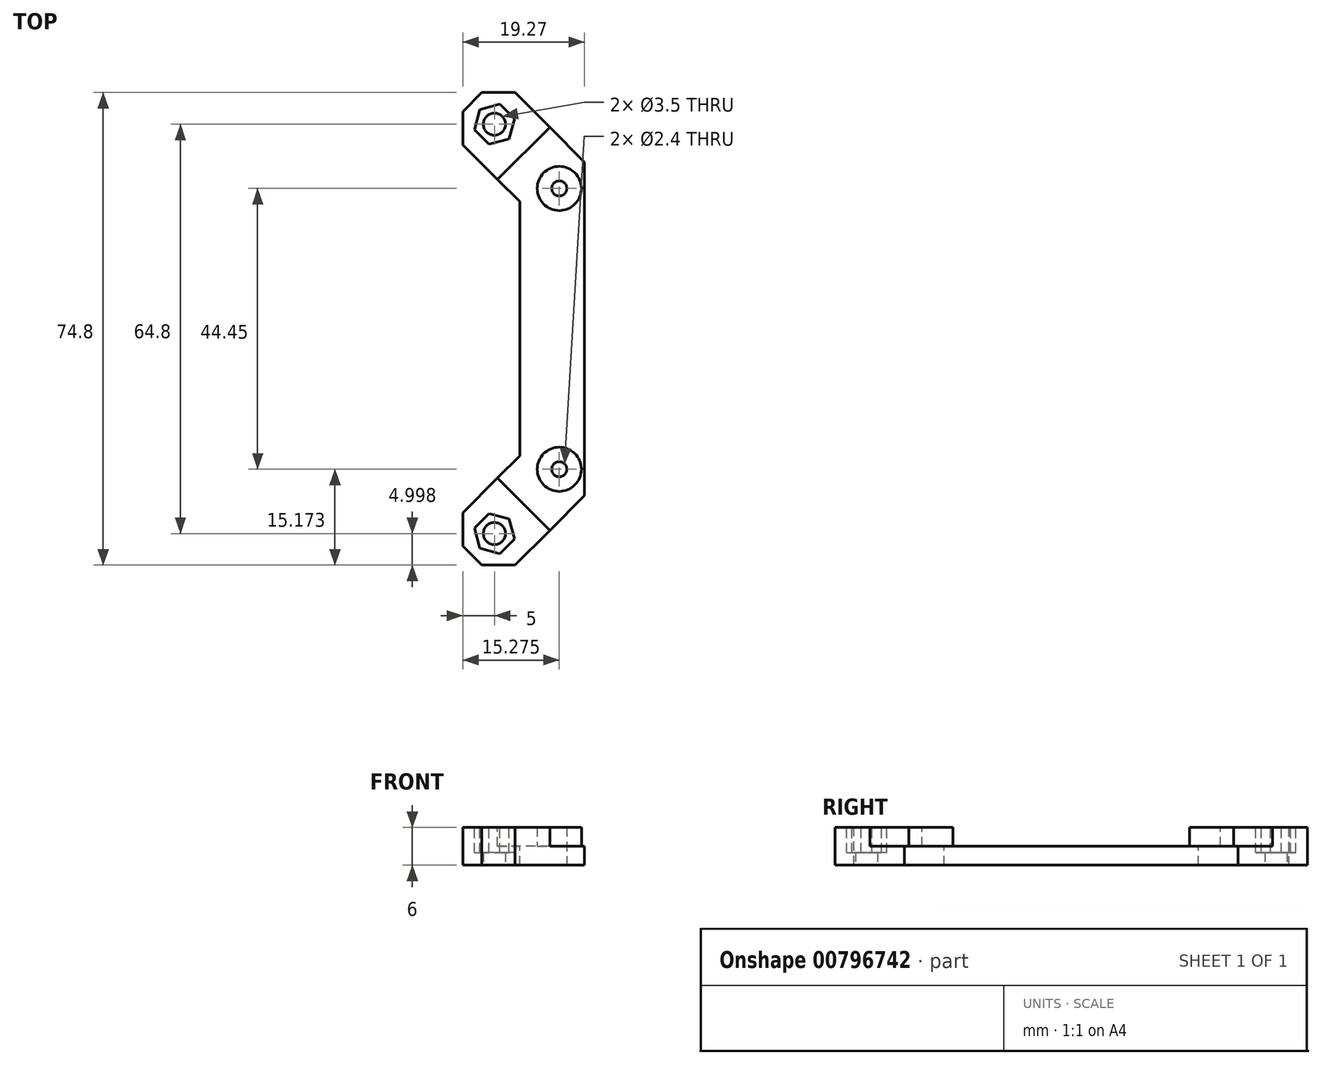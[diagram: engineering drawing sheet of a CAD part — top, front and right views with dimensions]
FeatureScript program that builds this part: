
annotation { "Feature Type Name" : "Feature", "Feature Type Description" : "" }
export const myFeature = defineFeature(function(context is Context, id is Id, definition is map)
    precondition{}
    {
        {
            var Q0;
            Q0=qCreatedBy(makeId("Top.planeOp"),FACE);
            var sketch = newSketch(context, id + "F0", { "sketchPlane" : qUnion([Q0])});
            skLineSegment(sketch, "E0.bottom", {"start": v(-40.3, 34.1) * mm, "end": v(54.94, 34.1) * mm, "construction": true});
            skLineSegment(sketch, "E0.top", {"start": v(-40.3, -10.36) * mm, "end": v(54.94, -10.36) * mm, "construction": true});
            skLineSegment(sketch, "E0.left", {"start": v(-40.3, 34.1) * mm, "end": v(-40.3, -10.36) * mm, "construction": true});
            skLineSegment(sketch, "E0.right", {"start": v(54.94, 34.1) * mm, "end": v(54.94, -10.36) * mm, "construction": true});
            skCircle(sketch, "E1", {"center": v(-40.3, -10.36) * mm, "radius": 1.2 * mm});
            skCircle(sketch, "E2", {"center": v(-40.3, 34.1) * mm, "radius": 1.2 * mm});
            skCircle(sketch, "E3", {"center": v(54.94, 34.1) * mm, "radius": 1.75 * mm});
            skCircle(sketch, "E4", {"center": v(54.94, -10.36) * mm, "radius": 1.75 * mm});
            skLineSegment(sketch, "E5.bottom", {"start": v(-50.58, 44.27) * mm, "end": v(65.22, 44.27) * mm, "construction": true});
            skLineSegment(sketch, "E5.top", {"start": v(-50.58, -20.53) * mm, "end": v(65.22, -20.53) * mm, "construction": true});
            skLineSegment(sketch, "E5.left", {"start": v(-50.58, 44.27) * mm, "end": v(-50.58, -20.53) * mm, "construction": true});
            skLineSegment(sketch, "E5.right", {"start": v(65.22, 44.27) * mm, "end": v(65.22, -20.53) * mm, "construction": true});
            skLineSegment(sketch, "E6", {"start": v(54.94, 11.87) * mm, "end": v(65.22, 11.87) * mm, "construction": true});
            skLineSegment(sketch, "E7", {"start": v(-50.58, 11.87) * mm, "end": v(-40.3, 11.87) * mm, "construction": true});
            skCircle(sketch, "E8", {"center": v(-50.58, -20.53) * mm, "radius": 1.75 * mm});
            skCircle(sketch, "E9", {"center": v(-50.58, 44.27) * mm, "radius": 1.75 * mm});
            skCircle(sketch, "E10", {"center": v(65.22, 44.27) * mm, "radius": 1.75 * mm});
            skCircle(sketch, "E11", {"center": v(65.22, -20.53) * mm, "radius": 1.75 * mm});
            skLineSegment(sketch, "E12", {"start": v(-55.58, 49.27) * mm, "end": v(-55.58, -25.53) * mm});
            skLineSegment(sketch, "E13", {"start": v(-55.58, -25.53) * mm, "end": v(-36.3, -25.53) * mm});
            skLineSegment(sketch, "E14", {"start": v(-36.3, -25.53) * mm, "end": v(-36.3, 49.27) * mm});
            skLineSegment(sketch, "E15", {"start": v(-36.3, 49.27) * mm, "end": v(-55.58, 49.27) * mm});
            skLineSegment(sketch, "E16", {"start": v(-55.58, 11.87) * mm, "end": v(-50.58, 11.87) * mm, "construction": true});
            skSolve(sketch);
        }
        {
            var Q0;
            Q0=makeQuery(id+"F0.imprint","IMPRINT",FACE,{"disambiguationData":[TD([[makeQuery(id+"F0.imprint","IMPRINT",EDGE,{"derivedFrom":sQuery(id+"F0.wireOp",EDGE,"E1")}),-1.0]])]});
            extrude(context, id + "F1", {"entities" : qUnion([Q0]), "depth" : 6 * mm, "offsetDistance" : 25 * mm});
        }
        {
            var Q0;
            Q0=makeQuery(id+"F1.opExtrude","CAP_FACE",FACE,{"disambiguationData":[OSD([sQuery(id+"F0.wireOp",EDGE,"E1"),sQuery(id+"F0.wireOp",EDGE,"E2"),sQuery(id+"F0.wireOp",EDGE,"E8"),sQuery(id+"F0.wireOp",EDGE,"E9"),sQuery(id+"F0.wireOp",EDGE,"E12"),sQuery(id+"F0.wireOp",EDGE,"E13"),sQuery(id+"F0.wireOp",EDGE,"E14"),sQuery(id+"F0.wireOp",EDGE,"E15")])],"isStart":false});
            var sketch = newSketch(context, id + "F2", { "sketchPlane" : qUnion([Q0])});
            skLineSegment(sketch, "E17", {"start": v(-55.58, -17.26) * mm, "end": v(-46.58, -8.26) * mm});
            skLineSegment(sketch, "E18", {"start": v(-46.58, -8.26) * mm, "end": v(-46.58, 32) * mm});
            skLineSegment(sketch, "E19", {"start": v(-46.58, 32) * mm, "end": v(-55.58, 41) * mm});
            skLineSegment(sketch, "E20", {"start": v(-46.58, 11.87) * mm, "end": v(-55.58, 11.87) * mm, "construction": true});
            skLineSegment(sketch, "E21", {"start": v(-36.3, 38.27) * mm, "end": v(-47.3, 49.27) * mm});
            skLineSegment(sketch, "E22", {"start": v(-47.3, -25.53) * mm, "end": v(-36.3, -14.53) * mm});
            skLineSegment(sketch, "E23", {"start": v(-41.8, 43.77) * mm, "end": v(-50.08, 35.5) * mm});
            skLineSegment(sketch, "E24", {"start": v(-41.8, -20.03) * mm, "end": v(-50.08, -11.76) * mm});
            skCircle(sketch, "E25.cCircle", {"center": v(-50.58, 44.27) * mm, "radius": 2.85 * mm, "construction": true});
            skLineSegment(sketch, "E25.0", {"start": v(-52.9, 46.6) * mm, "end": v(-49.73, 47.45) * mm});
            skLineSegment(sketch, "E25.1", {"start": v(-49.73, 47.45) * mm, "end": v(-47.4, 45.12) * mm});
            skLineSegment(sketch, "E25.2", {"start": v(-47.4, 45.12) * mm, "end": v(-48.25, 41.94) * mm});
            skLineSegment(sketch, "E25.3", {"start": v(-48.25, 41.94) * mm, "end": v(-51.43, 41.09) * mm});
            skLineSegment(sketch, "E25.4", {"start": v(-51.43, 41.09) * mm, "end": v(-53.76, 43.42) * mm});
            skLineSegment(sketch, "E25.5", {"start": v(-53.76, 43.42) * mm, "end": v(-52.9, 46.6) * mm});
            skPoint(sketch, "E25.0.midPoint", {"position": v(-51.32, 47.02) * mm});
            skLineSegment(sketch, "E26", {"start": v(-52.9, 46.6) * mm, "end": v(-55.58, 49.27) * mm, "construction": true});
            skCircle(sketch, "E27.cCircle", {"center": v(-50.58, -20.53) * mm, "radius": 2.85 * mm, "construction": true});
            skLineSegment(sketch, "E27.0", {"start": v(-49.73, -23.71) * mm, "end": v(-52.9, -22.86) * mm});
            skLineSegment(sketch, "E27.1", {"start": v(-52.9, -22.86) * mm, "end": v(-53.76, -19.68) * mm});
            skLineSegment(sketch, "E27.2", {"start": v(-53.76, -19.68) * mm, "end": v(-51.43, -17.35) * mm});
            skLineSegment(sketch, "E27.3", {"start": v(-51.43, -17.35) * mm, "end": v(-48.25, -18.2) * mm});
            skLineSegment(sketch, "E27.4", {"start": v(-48.25, -18.2) * mm, "end": v(-47.4, -21.38) * mm});
            skLineSegment(sketch, "E27.5", {"start": v(-47.4, -21.38) * mm, "end": v(-49.73, -23.71) * mm});
            skPoint(sketch, "E27.0.midPoint", {"position": v(-51.32, -23.28) * mm});
            skLineSegment(sketch, "E28", {"start": v(-52.9, -22.86) * mm, "end": v(-55.58, -25.53) * mm, "construction": true});
            skSolve(sketch);
        }
        {
            var Q0;
            {var subQ0=sQuery(id+"F2.wireOp",EDGE,"E21");var subQ1=makeQuery(id+"F1.opExtrude","CAP_EDGE",EDGE,{"disambiguationData":[OSD([sQuery(id+"F0.wireOp",EDGE,"E14")])],"isStart":false});var subQ2=makeQuery(id+"F2.imprint","INTERSECT",VERTEX,{"derivedFrom":[subQ1,subQ0]});Q0=makeQuery(id+"F2.imprint","IMPRINT",FACE,{"disambiguationData":[TD([[makeQuery(id+"F2.imprint","IMPRINT",EDGE,{"disambiguationData":[TD([[subQ2,-1.0]])],"derivedFrom":subQ0}),-1.0]])]});}
            var Q1;
            {var subQ1=sQuery(id+"F2.wireOp",EDGE,"E18");Q1=makeQuery(id+"F2.imprint","IMPRINT",FACE,{"disambiguationData":[TD([[makeQuery(id+"F2.imprint","IMPRINT",EDGE,{"derivedFrom":subQ1}),1.0]])]});}
            var Q2;
            {var subQ0=sQuery(id+"F2.wireOp",EDGE,"E22");var subQ1=makeQuery(id+"F1.opExtrude","CAP_EDGE",EDGE,{"disambiguationData":[OSD([sQuery(id+"F0.wireOp",EDGE,"E13")])],"isStart":false});var subQ2=makeQuery(id+"F2.imprint","INTERSECT",VERTEX,{"derivedFrom":[subQ1,subQ0]});Q2=makeQuery(id+"F2.imprint","IMPRINT",FACE,{"disambiguationData":[TD([[makeQuery(id+"F2.imprint","IMPRINT",EDGE,{"disambiguationData":[TD([[subQ2,-1.0]])],"derivedFrom":subQ0}),-1.0]])]});}
            extrude(context, id + "F3", {"entities" : qUnion([Q0, Q1, Q2]), "operationType" : NewBodyOperationType.REMOVE, "oppositeDirection" : true, "depth" : 25 * mm, "offsetDistance" : 25 * mm});
        }
        {
            var Q0;
            {var subQ5=sQuery(id+"F2.wireOp",EDGE,"E18");Q0=makeQuery(id+"F2.imprint","IMPRINT",FACE,{"disambiguationData":[TD([[makeQuery(id+"F2.imprint","IMPRINT",EDGE,{"derivedFrom":subQ5}),-1.0]])]});}
            var Q1;
            Q1=makeQuery(id+"F2.imprint","IMPRINT",FACE,{"disambiguationData":[TD([[makeQuery(id+"F2.imprint","IMPRINT",EDGE,{"derivedFrom":sQuery(id+"F2.wireOp",EDGE,"d42421a5-ac7b-4057-9577-e83b0d60c713.0")}),-1.0]])]});
            var Q2;
            Q2=makeQuery(id+"F2.imprint","IMPRINT",FACE,{"disambiguationData":[TD([[makeQuery(id+"F2.imprint","IMPRINT",EDGE,{"derivedFrom":sQuery(id+"F2.wireOp",EDGE,"defd8206-cf14-4cda-9da2-6035153b5954.0")}),-1.0]])]});
            extrude(context, id + "F4", {"entities" : qUnion([Q0, Q1, Q2]), "operationType" : NewBodyOperationType.REMOVE, "oppositeDirection" : true, "depth" : 3 * mm, "offsetDistance" : 25 * mm});
        }
        {
            var Q0;
            Q0=makeQuery(id+"F1.opExtrude","SWEPT_EDGE",EDGE,{"disambiguationData":[OSD([sQuery(id+"F0.wireOp",EDGE,"E12"),sQuery(id+"F0.wireOp",EDGE,"E15")])]});
            var Q1;
            Q1=makeQuery(id+"F1.opExtrude","SWEPT_EDGE",EDGE,{"disambiguationData":[OSD([sQuery(id+"F0.wireOp",EDGE,"E12"),sQuery(id+"F0.wireOp",EDGE,"E13")])]});
            chamfer(context, id + "F5", {"entities" : qUnion([Q0, Q1]), "width" : 3 * mm, "tangentPropagation" : true});
        }
        {
            var Q0;
            Q0=makeQuery(id+"F2.imprint","IMPRINT",FACE,{"disambiguationData":[TD([[makeQuery(id+"F2.imprint","IMPRINT",EDGE,{"derivedFrom":sQuery(id+"F2.wireOp",EDGE,"E25.0")}),-1.0]])]});
            var Q1;
            Q1=makeQuery(id+"F2.imprint","IMPRINT",FACE,{"disambiguationData":[TD([[makeQuery(id+"F2.imprint","IMPRINT",EDGE,{"derivedFrom":sQuery(id+"F2.wireOp",EDGE,"E27.0")}),-1.0]])]});
            extrude(context, id + "F6", {"entities" : qUnion([Q0, Q1]), "operationType" : NewBodyOperationType.REMOVE, "oppositeDirection" : true, "depth" : 4 * mm, "offsetDistance" : 25 * mm});
        }
        {
            var Q0;
            Q0=makeQuery(id+"F4.boolean.opBoolean","COPY",FACE,{"derivedFrom":makeQuery(id+"F4.opExtrude","CAP_FACE",FACE,{"disambiguationData":[OSD([sQuery(id+"F0.wireOp",EDGE,"E1"),sQuery(id+"F0.wireOp",EDGE,"E2"),sQuery(id+"F0.wireOp",EDGE,"E14"),sQuery(id+"F2.wireOp",EDGE,"E17"),sQuery(id+"F2.wireOp",EDGE,"E18"),sQuery(id+"F2.wireOp",EDGE,"E19"),sQuery(id+"F2.wireOp",EDGE,"E21"),sQuery(id+"F2.wireOp",EDGE,"E22"),sQuery(id+"F2.wireOp",EDGE,"E23"),sQuery(id+"F2.wireOp",EDGE,"E24")])],"isStart":false})});
            var sketch = newSketch(context, id + "F7", { "sketchPlane" : qUnion([Q0])});
            skCircle(sketch, "E29", {"center": v(-40.3, 34.1) * mm, "radius": 3.5 * mm});
            skCircle(sketch, "E30", {"center": v(-40.3, -10.36) * mm, "radius": 3.5 * mm});
            skSolve(sketch);
        }
        {
            var Q0;
            Q0=makeQuery(id+"F7.imprint","IMPRINT",FACE,{"disambiguationData":[TD([[makeQuery(id+"F7.imprint","IMPRINT",EDGE,{"derivedFrom":sQuery(id+"F7.wireOp",EDGE,"E30")}),1.0]])]});
            var Q1;
            Q1=makeQuery(id+"F7.imprint","IMPRINT",FACE,{"disambiguationData":[TD([[makeQuery(id+"F7.imprint","IMPRINT",EDGE,{"derivedFrom":sQuery(id+"F7.wireOp",EDGE,"E29")}),1.0]])]});
            extrude(context, id + "F8", {"entities" : qUnion([Q0, Q1]), "operationType" : NewBodyOperationType.ADD, "depth" : 3 * mm, "offsetDistance" : 25 * mm});
        }
    });
